# Revit family: IS_UltraflatII_T4490_BIM_NL
name_source: partatom
category: Plumbing Fixtures
revit_build: Autodesk Revit 2017 (Build: 20160225_1515(x64)
units: mm (PartAtom-declared; Revit-internal decimal feet)

## family parameters
Always vertical = No
Cut with Voids When Loaded = No
OmniClass Number = 23.45.05.14.17
OmniClass Title = Showers
Part Type = Normal
Room Calculation Point = No
Round Connector Dimension = Use Diameter
Shared = No
Work Plane-Based = No

## types (2) — shared parameters
Accesoires = https://www.idealstandardnederland.nl
Accessories = https://www.idealstandardnederland.nl
Afmetingen = 1400 x 1000 x 25 mm
Artikelomschrijving = Ultra-Flat 2 Duschwanne 1400 x 1000mm, Rechteckig. Erhältlich in 2 fertigen Weiß und Satin Weiß.
Artikelreferentie = ULTRAFLAT 2 SHT 140X100 RECT WHITE
Auteur = Ideal Standard
BIMObjectName = IS_IdealStandard_ShowerTrays_UltraFlat2_T4490
BIMobject category code = sanitary-shower-trays
BIMobject main category = Sanitary
BIMobject main category code = sanitary
Beschrijvinggarantie = fabrieksgarantie
BimObjectNaam = IS_IdealStandard_ShowerTrays_UltraFlat2_T4490
Brand = Ideal Standard GmbH
Brand url = https://www.idealstandardnederland.nl
Breedte = 1400.000061
ConnectionType = Plumbing
CurrencyUnit = €
CurrentRevision = 1
Date of publishing = 15/12/2020
Diepte = 1000 mm
Douchebak = No
DurationUnit = Years
DuurEenheid = Jaren
Duurzaamheid = 5
Edition number = 1
Eigenschappen = Duschwanne 1400 x 1000mm, Rechteckig. Erhältlich in 2 fertigen Weiß und Satin Weiß.
Garantieonderdelen = 5
Garantieunits = Jaren
Heefthandvaten = No
Hoogte = 24.906805
IFC Classification = Sanitary Terminal
IfcExportAs = IfcSanitaryTerminalType
IfcExportType = SHOWERTRAY
Installatieinstructies = https://www.idealstandardnederland.nl
Installation instructions = https://www.idealstandardnederland.nl
InstallationInstructions = https://www.idealstandardnederland.nl
IsAutomaticFlush = No
IsBuiltIn = No
IsHighPressure = No
IsSingleFlush = No
Lengte = 1000 mm
LinearUnits = millimetres
MainColor = White
MaintenanceInformation = https://www.idealstandardnederland.nl
Manufacturer = Ideal Standard Netherlands
Manufacturer name = Ideal Standard
ManufacturerURL = https://www.idealstandardnederland.nl
Masterformat 2014 Code = 10 21 16
Masterformat 2014 Description = Shower and Dressing compartements
Materiaal = hars
Material = Resin
Material main = Resin
Merk = Ideal Standard GmbH
Montageinstuctie = https://www.idealstandardnederland.nl
NBS Reference Code = 45-35-70/336
NBS Reference Description = Shower trays
Name = ShowerTrays_UltraFlat2_T4490_IdealStandard
NettWeight = 23.4 Kg
NominalDepth = 1000 mm
NominalHeight = 25 mm
NominalLength = 1000 mm
NominalWidth = 1400 mm
Normen = ShowerTrays_UltraFlat2_T4490_IdealStandard
OmniClass Code = 23-15 11 15 13
OmniClass Description = Shower and Dressing Compartments
OppervlakteEenheid = millimeter
Product Guid = c29b49e3-e6dd-4e54-9543-fe619537cd3a
Product SKU = T4490
Product data url = https://bimobject.com
Product family = ULTRA FLAT
Product group = Shower Tray
Product name = ULTRAFLAT 2 SHT 140X100 RECT WHITE
Product url = https://www.idealstandardnederland.nl
ProductInformation = https://www.idealstandardnederland.nl
Productinformatie = https://www.idealstandardnederland.nl
QR code = https://www.idealstandardnederland.nl
Referentie = ULTRAFLAT 2 SHT 140X100 RECT WHITE
Revisie = 1
Shape = Rectangular
Size = 1400 x 1000 x 25 mm
Space = Internal
Technical description = https://www.idealstandardnederland.nl
Telefoonnummer = (077) 355 08 08
Typeconnectie = loodgieter
UNSPSC Code = 301815
URL = https://www.idealstandard.nl
Uniclass 1.4 Code = L72143
Uniclass 1.4 Description = Shower trays
Uniclass 2.0 Code = PR-35-06-84
Uniclass 2.0 Description = Shower Trays
Uniclass 2015 Code = Pr_40_20_06_84
Uniclass 2015 Name = Shower trays
Uniclass2015Beschrijving = Pr_40_20_06_84
Uniclass2015Code = Pr_40_20_06_84
Uniclass2015Referentie = Shower trays
Uniclass2015Title = Shower trays
Uniclass2015Version = v1.20
Urlproducent = https://www.idealstandard.nl
ValutaEenheid = €
Versie = 1
Version = 1
VolumeUnits = Litres
Volumeunits = Liter
Vorm = rechthoekig
WRASURL = https://www.wras.co.uk
WarrantyDescription = Manufacturers Warranty
WarrantyDurationParts = 25
WarrantyDurationUnit = Years
Wisselstukken = https://www.idealstandardnederland.nl
zero-valued in all types: BrutoGewicht, DrainSize, GrootteAfvoergat, InletConnectionSize, MaterialThickness, Nettogewicht, OutletConnectionSize, Overloop, Vervangingskosten

## per-type parameters (varying)
| type | Afwerking | Artikelnummer | BarCode | Barcode | Color | Description | Features | Finish | GTIN code | Kleur | Model | ModelNumber | ModelReference |
| T449001 - ULTRAFLAT 2 SHT 140X100 RECT GLOSSY WHITE | Glanzend wit | T449001 | 8014140482260 | 8014140482260 | Glossy White | Ultraflat2 Shower Tray 1400 x 1000mm, Rectangular with Glossy White Finish. | Shower Tray 1400 x 1000mm, Rectangular with Glossy White Finish. | Glossy White | 8014140482260 | Glanzend wit | T449001 | T449001 | ULTRAFLAT 2 SHT 140X100 RECT WHITE |
| T4490V1 - ULTRAFLAT 2 SHT 140X100 RECT SILK WHITE | Zijde wit | T4490V1 | 8014140482277 | 8014140482277 | Silk White | Ultraflat2 Shower Tray 1400 x 1000mm, Rectangular with Silk White Finish. | Shower Tray 1400 x 1000mm, Rectangular with Silk White Finish. | Silk White | 8014140482277 | Zijde wit | T4490V1 | T4490V1 | ULTRAFLAT 2 SHT 140X100 RECT SILK WHITE |

## geometry (parser evidence)
native form markers: Sweep x4
no freeform markers — native parametric forms only
